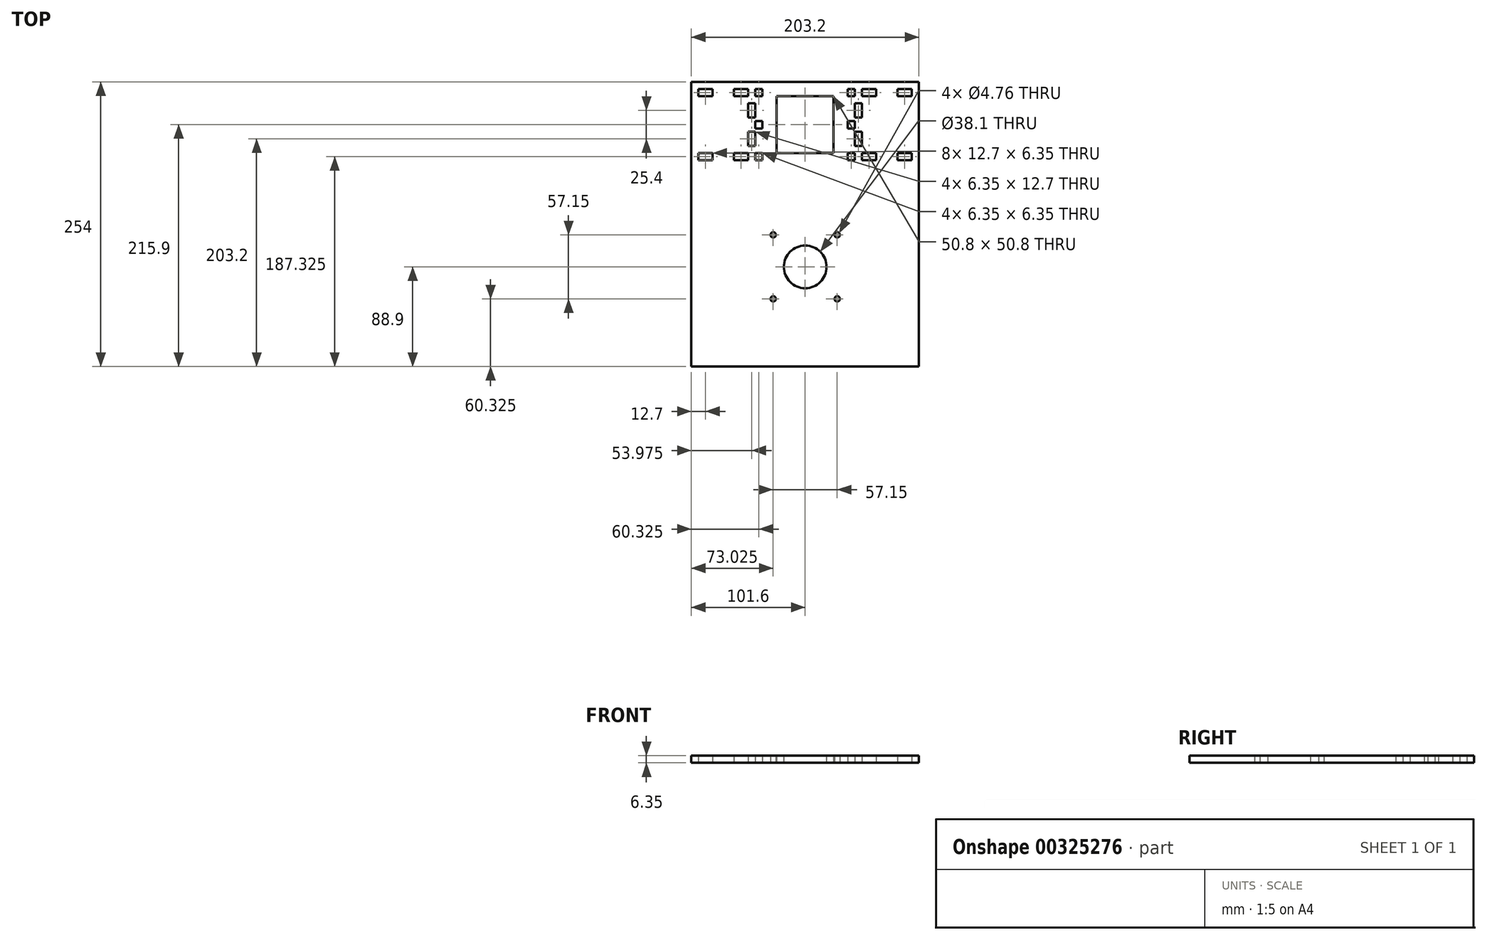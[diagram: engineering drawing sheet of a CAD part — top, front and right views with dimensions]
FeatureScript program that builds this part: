
annotation { "Feature Type Name" : "Feature", "Feature Type Description" : "" }
export const myFeature = defineFeature(function(context is Context, id is Id, definition is map)
    precondition{}
    {
        {
            var Q0;
            Q0=qCreatedBy(makeId("Top.planeOp"),FACE);
            var sketch = newSketch(context, id + "F0", { "sketchPlane" : qUnion([Q0])});
            skLineSegment(sketch, "E0.bottom", {"start": v(0, 0) * mm, "end": v(203.2, 0) * mm});
            skLineSegment(sketch, "E0.top", {"start": v(0, 254) * mm, "end": v(203.2, 254) * mm});
            skLineSegment(sketch, "E0.left", {"start": v(0, 0) * mm, "end": v(0, 254) * mm});
            skLineSegment(sketch, "E0.right", {"start": v(203.2, 0) * mm, "end": v(203.2, 254) * mm});
            skLineSegment(sketch, "E1.bottom", {"start": v(76.2, 241.3) * mm, "end": v(127, 241.3) * mm});
            skLineSegment(sketch, "E1.top", {"start": v(76.2, 190.5) * mm, "end": v(127, 190.5) * mm});
            skLineSegment(sketch, "E1.left", {"start": v(76.2, 241.3) * mm, "end": v(76.2, 190.5) * mm});
            skLineSegment(sketch, "E1.right", {"start": v(127, 241.3) * mm, "end": v(127, 190.5) * mm});
            skLineSegment(sketch, "E2.bottom", {"start": v(6.35, 247.65) * mm, "end": v(19.05, 247.65) * mm});
            skLineSegment(sketch, "E2.top", {"start": v(6.35, 241.3) * mm, "end": v(19.05, 241.3) * mm});
            skLineSegment(sketch, "E2.left", {"start": v(6.35, 247.65) * mm, "end": v(6.35, 241.3) * mm});
            skLineSegment(sketch, "E2.right", {"start": v(19.05, 247.65) * mm, "end": v(19.05, 241.3) * mm});
            skLineSegment(sketch, "E3.bottom", {"start": v(38.1, 247.65) * mm, "end": v(50.8, 247.65) * mm});
            skLineSegment(sketch, "E3.top", {"start": v(38.1, 241.3) * mm, "end": v(50.8, 241.3) * mm});
            skLineSegment(sketch, "E3.left", {"start": v(38.1, 247.65) * mm, "end": v(38.1, 241.3) * mm});
            skLineSegment(sketch, "E3.right", {"start": v(50.8, 247.65) * mm, "end": v(50.8, 241.3) * mm});
            skLineSegment(sketch, "E4", {"start": v(127, 215.9) * mm, "end": v(0, 215.9) * mm, "construction": true});
            skLineSegment(sketch, "E5", {"start": v(0, 215.9) * mm, "end": v(203.2, 215.9) * mm, "construction": true});
            skLineSegment(sketch, "E6", {"start": v(101.6, 254) * mm, "end": v(101.6, 0) * mm, "construction": true});
            skLineSegment(sketch, "E7.MirrorCS", {"start": v(6.35, 184.15) * mm, "end": v(6.35, 190.5) * mm});
            skLineSegment(sketch, "E8.MirrorCS", {"start": v(38.1, 190.5) * mm, "end": v(50.8, 190.5) * mm});
            skLineSegment(sketch, "E9.MirrorCS", {"start": v(19.05, 184.15) * mm, "end": v(19.05, 190.5) * mm});
            skLineSegment(sketch, "E10.MirrorCS", {"start": v(50.8, 184.15) * mm, "end": v(50.8, 190.5) * mm});
            skLineSegment(sketch, "E11.MirrorCS", {"start": v(38.1, 184.15) * mm, "end": v(38.1, 190.5) * mm});
            skLineSegment(sketch, "E12.MirrorCS", {"start": v(38.1, 184.15) * mm, "end": v(50.8, 184.15) * mm});
            skLineSegment(sketch, "E13.MirrorCS", {"start": v(6.35, 190.5) * mm, "end": v(19.05, 190.5) * mm});
            skLineSegment(sketch, "E14.MirrorCS", {"start": v(6.35, 184.15) * mm, "end": v(19.05, 184.15) * mm});
            skLineSegment(sketch, "E15.MirrorCS", {"start": v(76.2, 215.9) * mm, "end": v(203.2, 215.9) * mm, "construction": true});
            skLineSegment(sketch, "E16.MirrorCS", {"start": v(203.2, 215.9) * mm, "end": v(0, 215.9) * mm, "construction": true});
            skLineSegment(sketch, "E17.MirrorCS", {"start": v(165.1, 184.15) * mm, "end": v(152.4, 184.15) * mm});
            skLineSegment(sketch, "E18.MirrorCS", {"start": v(165.1, 184.15) * mm, "end": v(165.1, 190.5) * mm});
            skLineSegment(sketch, "E19.MirrorCS", {"start": v(196.85, 241.3) * mm, "end": v(184.15, 241.3) * mm});
            skLineSegment(sketch, "E20.MirrorCS", {"start": v(165.1, 247.65) * mm, "end": v(165.1, 241.3) * mm});
            skLineSegment(sketch, "E21.MirrorCS", {"start": v(165.1, 241.3) * mm, "end": v(152.4, 241.3) * mm});
            skLineSegment(sketch, "E22.MirrorCS", {"start": v(196.85, 247.65) * mm, "end": v(196.85, 241.3) * mm});
            skLineSegment(sketch, "E23.MirrorCS", {"start": v(152.4, 247.65) * mm, "end": v(152.4, 241.3) * mm});
            skLineSegment(sketch, "E24.MirrorCS", {"start": v(184.15, 247.65) * mm, "end": v(184.15, 241.3) * mm});
            skLineSegment(sketch, "E25.MirrorCS", {"start": v(152.4, 184.15) * mm, "end": v(152.4, 190.5) * mm});
            skLineSegment(sketch, "E26.MirrorCS", {"start": v(184.15, 184.15) * mm, "end": v(184.15, 190.5) * mm});
            skLineSegment(sketch, "E27.MirrorCS", {"start": v(196.85, 247.65) * mm, "end": v(184.15, 247.65) * mm});
            skLineSegment(sketch, "E28.MirrorCS", {"start": v(196.85, 184.15) * mm, "end": v(196.85, 190.5) * mm});
            skLineSegment(sketch, "E29.MirrorCS", {"start": v(196.85, 184.15) * mm, "end": v(184.15, 184.15) * mm});
            skLineSegment(sketch, "E30.MirrorCS", {"start": v(165.1, 247.65) * mm, "end": v(152.4, 247.65) * mm});
            skLineSegment(sketch, "E31.MirrorCS", {"start": v(196.85, 190.5) * mm, "end": v(184.15, 190.5) * mm});
            skLineSegment(sketch, "E32.MirrorCS", {"start": v(165.1, 190.5) * mm, "end": v(152.4, 190.5) * mm});
            skLineSegment(sketch, "E33.MirrorCS", {"start": v(101.6, 177.8) * mm, "end": v(101.6, 431.8) * mm, "construction": true});
            skLineSegment(sketch, "E34", {"start": v(0, 88.9) * mm, "end": v(203.2, 88.9) * mm, "construction": true});
            skCircle(sketch, "E35", {"center": v(73.02, 117.48) * mm, "radius": 2.38 * mm});
            skCircle(sketch, "E36.MirrorC", {"center": v(130.18, 117.48) * mm, "radius": 2.38 * mm});
            skLineSegment(sketch, "E37.MirrorCS", {"start": v(203.2, 88.9) * mm, "end": v(0, 88.9) * mm, "construction": true});
            skCircle(sketch, "E38.MirrorC", {"center": v(130.18, 60.32) * mm, "radius": 2.38 * mm});
            skCircle(sketch, "E39.MirrorC", {"center": v(73.02, 60.32) * mm, "radius": 2.38 * mm});
            skCircle(sketch, "E40", {"center": v(101.6, 88.9) * mm, "radius": 19.05 * mm});
            skLineSegment(sketch, "E41.bottom", {"start": v(50.8, 234.95) * mm, "end": v(57.15, 234.95) * mm});
            skLineSegment(sketch, "E41.top", {"start": v(50.8, 222.25) * mm, "end": v(57.15, 222.25) * mm});
            skLineSegment(sketch, "E41.left", {"start": v(50.8, 234.95) * mm, "end": v(50.8, 222.25) * mm});
            skLineSegment(sketch, "E41.right", {"start": v(57.15, 234.95) * mm, "end": v(57.15, 222.25) * mm});
            skLineSegment(sketch, "E42.MirrorCS", {"start": v(50.8, 196.85) * mm, "end": v(57.15, 196.85) * mm});
            skLineSegment(sketch, "E43.MirrorCS", {"start": v(57.15, 196.85) * mm, "end": v(57.15, 209.55) * mm});
            skLineSegment(sketch, "E44.MirrorCS", {"start": v(50.8, 209.55) * mm, "end": v(57.15, 209.55) * mm});
            skLineSegment(sketch, "E45.MirrorCS", {"start": v(50.8, 196.85) * mm, "end": v(50.8, 209.55) * mm});
            skLineSegment(sketch, "E46.MirrorCS", {"start": v(152.4, 234.95) * mm, "end": v(146.05, 234.95) * mm});
            skLineSegment(sketch, "E47.MirrorCS", {"start": v(152.4, 196.85) * mm, "end": v(146.05, 196.85) * mm});
            skLineSegment(sketch, "E48.MirrorCS", {"start": v(152.4, 209.55) * mm, "end": v(146.05, 209.55) * mm});
            skLineSegment(sketch, "E49.MirrorCS", {"start": v(152.4, 222.25) * mm, "end": v(146.05, 222.25) * mm});
            skLineSegment(sketch, "E50.MirrorCS", {"start": v(152.4, 196.85) * mm, "end": v(152.4, 209.55) * mm});
            skLineSegment(sketch, "E51.MirrorCS", {"start": v(146.05, 234.95) * mm, "end": v(146.05, 222.25) * mm});
            skLineSegment(sketch, "E52.MirrorCS", {"start": v(146.05, 196.85) * mm, "end": v(146.05, 209.55) * mm});
            skLineSegment(sketch, "E53.MirrorCS", {"start": v(152.4, 234.95) * mm, "end": v(152.4, 222.25) * mm});
            skLineSegment(sketch, "E54.bottom", {"start": v(57.15, 241.3) * mm, "end": v(63.5, 241.3) * mm});
            skLineSegment(sketch, "E54.top", {"start": v(57.15, 247.65) * mm, "end": v(63.5, 247.65) * mm});
            skLineSegment(sketch, "E54.left", {"start": v(57.15, 241.3) * mm, "end": v(57.15, 247.65) * mm});
            skLineSegment(sketch, "E54.right", {"start": v(63.5, 241.3) * mm, "end": v(63.5, 247.65) * mm});
            skLineSegment(sketch, "E55.bottom", {"start": v(57.15, 219.08) * mm, "end": v(63.5, 219.08) * mm});
            skLineSegment(sketch, "E55.top", {"start": v(57.15, 212.5) * mm, "end": v(63.5, 212.5) * mm});
            skLineSegment(sketch, "E55.left", {"start": v(57.15, 219.08) * mm, "end": v(57.15, 212.5) * mm});
            skLineSegment(sketch, "E55.right", {"start": v(63.5, 219.08) * mm, "end": v(63.5, 212.5) * mm});
            skLineSegment(sketch, "E56.MirrorCS", {"start": v(57.15, 184.15) * mm, "end": v(63.5, 184.15) * mm});
            skLineSegment(sketch, "E57.MirrorCS", {"start": v(57.15, 190.5) * mm, "end": v(57.15, 184.15) * mm});
            skLineSegment(sketch, "E58.MirrorCS", {"start": v(57.15, 190.5) * mm, "end": v(63.5, 190.5) * mm});
            skLineSegment(sketch, "E59.MirrorCS", {"start": v(63.5, 190.5) * mm, "end": v(63.5, 184.15) * mm});
            skLineSegment(sketch, "E60.MirrorCS", {"start": v(146.05, 241.3) * mm, "end": v(139.7, 241.3) * mm});
            skLineSegment(sketch, "E61.MirrorCS", {"start": v(146.05, 241.3) * mm, "end": v(146.05, 247.65) * mm});
            skLineSegment(sketch, "E62.MirrorCS", {"start": v(139.7, 241.3) * mm, "end": v(139.7, 247.65) * mm});
            skLineSegment(sketch, "E63.MirrorCS", {"start": v(146.05, 247.65) * mm, "end": v(139.7, 247.65) * mm});
            skLineSegment(sketch, "E64.MirrorCS", {"start": v(146.05, 219.08) * mm, "end": v(139.7, 219.08) * mm});
            skLineSegment(sketch, "E65.MirrorCS", {"start": v(146.05, 212.5) * mm, "end": v(139.7, 212.5) * mm});
            skLineSegment(sketch, "E66.MirrorCS", {"start": v(146.05, 219.08) * mm, "end": v(146.05, 212.5) * mm});
            skLineSegment(sketch, "E67.MirrorCS", {"start": v(139.7, 219.08) * mm, "end": v(139.7, 212.5) * mm});
            skLineSegment(sketch, "E68.MirrorCS", {"start": v(146.05, 190.5) * mm, "end": v(146.05, 184.15) * mm});
            skLineSegment(sketch, "E69.MirrorCS", {"start": v(139.7, 190.5) * mm, "end": v(139.7, 184.15) * mm});
            skLineSegment(sketch, "E70.MirrorCS", {"start": v(146.05, 190.5) * mm, "end": v(139.7, 190.5) * mm});
            skLineSegment(sketch, "E71.MirrorCS", {"start": v(146.05, 184.15) * mm, "end": v(139.7, 184.15) * mm});
            skSolve(sketch);
        }
        {
            var Q0;
            Q0=makeQuery(id+"F0.imprint","IMPRINT",FACE,{"disambiguationData":[TD([[makeQuery(id+"F0.imprint","IMPRINT",EDGE,{"derivedFrom":sQuery(id+"F0.wireOp",EDGE,"E0.bottom")}),1.0]])]});
            extrude(context, id + "F1", {"entities" : qUnion([Q0]), "depth" : 6.35 * mm});
        }
    });
